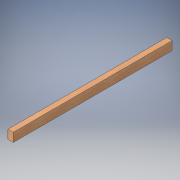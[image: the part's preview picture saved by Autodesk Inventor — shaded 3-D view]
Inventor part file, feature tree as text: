
AUTODESK INVENTOR PART (.ipt)
format: ipt  version: 2016 SP1 (Build 200210100, 210)  size: 95,232 bytes
history: native  units: in
note: dims shown in document units (in); Inventor stores cm internally (conversion verified against a paired STEP export)
features: extrude x1, sketch x1
ambient origin geometry x8: Origin, YZ Plane, XZ Plane, XY Plane, X Axis, Y Axis, Z Axis, Center Point
bodies: Solid1 (feature_tree)
feature tree (2):
  extrude  "Extrusion1"  Depth=2.5in
  sketch  "Sketch2"  dims[d2=1.5in d3=2.5in d4=45.0in d5=0.0in]
